# Revit family: EBRME-LED-414x-840-MPx
name_source: partatom
category: Leuchten
units: mm (PartAtom-declared; Revit-internal decimal feet)

## family parameters
Basisbauteil = Fläche
Beim Laden mit Abzugskörper schneiden = Nein
Bemaßung runder Anschluss = Durchmesser verwenden
Gemeinsam genutzt = Nein
Lichtquelle = Ja
OmniClass-Nummer = 23.80.70.11
OmniClass-Titel = Luminaries for Internal Lighting
Raumberechnungspunkt = Nein
Teiletyp = Normal

## types (8) — shared parameters
Baugruppenkennzeichen = D5020200
Emissionsform beim Rendern sichtbar = Nein
Farbfilter = 16777215
Farbtemperaturverschiebung bei Dämpfen der Lampe = <Keine Auswahl>
Hersteller = RIDI Leuchten GmbH
Lampe = LED
Neigungswinkel = 90.00°
URL = www.ridi.de
Von Breite des Rechtecks ausssenden = 534 mm  [stored 1.75197 ft]
Von Länge des Rechtecks aussenden = 532 mm  [stored 1.74541 ft]
brand = RIDI
conformity mark = CE
electrical safety class = 1
height = 66 mm  [stored 0.216535 ft]
length = 597 mm
nominal frequency = 50-60Hz
nominal voltage = 230
voltage type (AC, DC, UC) = AC
weight = 6,2 kg
width = 597 mm
zero-valued in all types: Vorgabe-Ansicht

## per-type parameters (varying)
| type | Datei für fotometrisches Netz | Modell | Scheinlast | ingress protection (IP) code | rated input power |
| EBRME-LED 414/5200-840 MPSD | EBRE-LED 4145200-840 MPSD.IES | 0822923 | 32 VA | IP54 | 32 |
| EBRME-LED 414/5200-840 MPSD-DA | EBRE-LED 4145200-840 MPSD.IES | 0832923 | 32 VA | IP54 | 32 |
| EBRME-LED 414/5200-840 MPSR | EBRE-LED 4145200-840 MPSR.IES | 0822922 | 32 VA | IP20 | 32 |
| EBRME-LED 414/5200-840 MPSR-DA | EBRE-LED 4145200-840 MPSR.IES | 0832922 | 32 VA | IP20 | 32 |
| EBRME-LED 414/6200-840 MPOD | EBRE-LED 4146200-840 MPOD.IES | 0822921 | 39 VA | IP54 | 39 |
| EBRME-LED 414/6200-840 MPOD-DA | EBRE-LED 4146200-840 MPOD.IES | 0832921 | 39 VA | IP54 | 39 |
| EBRME-LED 414/6200-840 MPOR | EBRE-LED 4146200-840 MPOR.IES | 0822920 | 39 VA | IP20 | 39 |
| EBRME-LED 414/6200-840 MPOR-DA | EBRE-LED 4146200-840 MPOR.IES | 0832920 | 39 VA | IP20 | 39 |

note: column(s) folded — value = type name in every type: product name

note: [stored X ft] marks values corroborated as IEEE doubles in the binary element streams (Revit-internal decimal feet)
